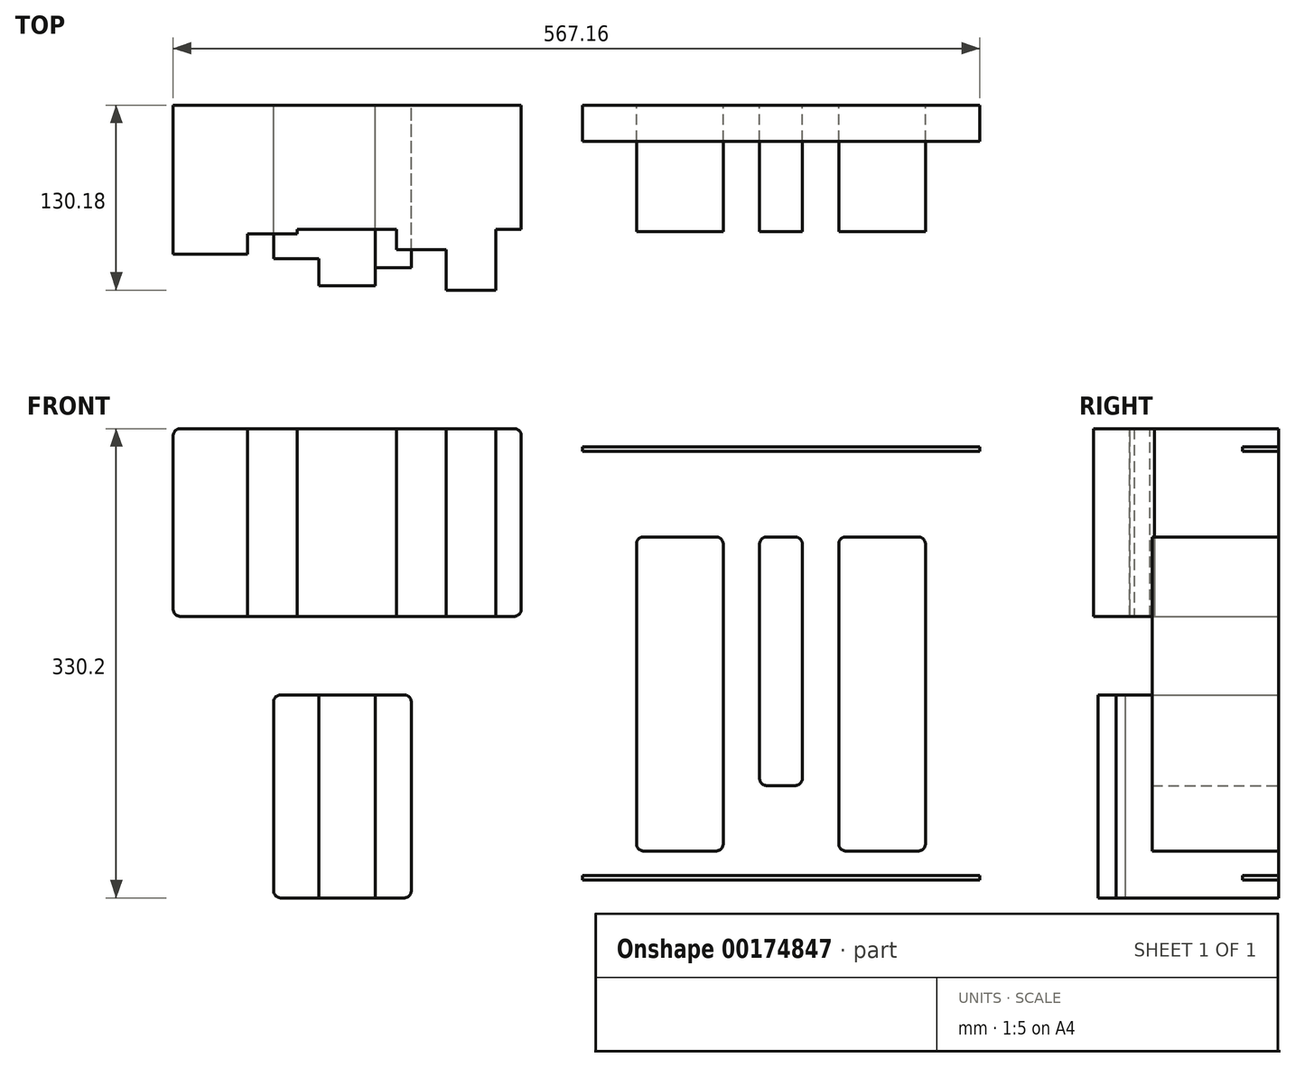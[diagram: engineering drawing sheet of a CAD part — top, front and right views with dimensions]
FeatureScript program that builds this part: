
annotation { "Feature Type Name" : "Feature", "Feature Type Description" : "" }
export const myFeature = defineFeature(function(context is Context, id is Id, definition is map)
    precondition{}
    {
        {
            var Q0;
            Q0=qCreatedBy(makeId("Front.planeOp"),FACE);
            var sketch = newSketch(context, id + "F0", { "sketchPlane" : qUnion([Q0])});
            skLineSegment(sketch, "E0.bottom", {"start": v(402.06, -139.7) * mm, "end": v(463.02, -139.7) * mm});
            skLineSegment(sketch, "E0.top", {"start": v(402.06, -360.68) * mm, "end": v(463.02, -360.68) * mm});
            skLineSegment(sketch, "E0.left", {"start": v(402.06, -139.7) * mm, "end": v(402.06, -360.68) * mm});
            skLineSegment(sketch, "E0.right", {"start": v(463.02, -139.7) * mm, "end": v(463.02, -360.68) * mm});
            skLineSegment(sketch, "E1.bottom", {"start": v(544.3, -139.7) * mm, "end": v(605.26, -139.7) * mm});
            skLineSegment(sketch, "E1.top", {"start": v(544.3, -360.68) * mm, "end": v(605.26, -360.68) * mm});
            skLineSegment(sketch, "E1.left", {"start": v(544.3, -139.7) * mm, "end": v(544.3, -360.68) * mm});
            skLineSegment(sketch, "E1.right", {"start": v(605.26, -139.7) * mm, "end": v(605.26, -360.68) * mm});
            skLineSegment(sketch, "E2.bottom", {"start": v(488.67, -139.7) * mm, "end": v(518.64, -139.7) * mm});
            skLineSegment(sketch, "E2.top", {"start": v(488.67, -314.7) * mm, "end": v(518.64, -314.7) * mm});
            skLineSegment(sketch, "E2.left", {"start": v(488.67, -139.7) * mm, "end": v(488.67, -314.7) * mm});
            skLineSegment(sketch, "E2.right", {"start": v(518.64, -139.7) * mm, "end": v(518.64, -314.7) * mm});
            skLineSegment(sketch, "E3.bottom", {"start": v(0, 0) * mm, "end": v(736.6, 0) * mm, "construction": true});
            skLineSegment(sketch, "E3.top", {"start": v(0, -457.2) * mm, "end": v(736.6, -457.2) * mm, "construction": true});
            skLineSegment(sketch, "E3.left", {"start": v(0, 0) * mm, "end": v(0, -457.2) * mm, "construction": true});
            skLineSegment(sketch, "E3.right", {"start": v(736.6, 0) * mm, "end": v(736.6, -457.2) * mm, "construction": true});
            skLineSegment(sketch, "E4.right", {"start": v(128.59, -195.58) * mm, "end": v(128.59, -63.5) * mm});
            skLineSegment(sketch, "E5.bottom", {"start": v(128.59, -63.5) * mm, "end": v(163.51, -63.5) * mm});
            skLineSegment(sketch, "E5.top", {"start": v(128.59, -195.58) * mm, "end": v(163.51, -195.58) * mm});
            skLineSegment(sketch, "E5.left", {"start": v(128.59, -63.5) * mm, "end": v(128.59, -195.58) * mm});
            skLineSegment(sketch, "E5.right", {"start": v(163.51, -63.5) * mm, "end": v(163.51, -195.58) * mm});
            skLineSegment(sketch, "E6.bottom", {"start": v(163.51, -63.5) * mm, "end": v(233.36, -63.5) * mm});
            skLineSegment(sketch, "E6.top", {"start": v(163.51, -195.58) * mm, "end": v(233.36, -195.58) * mm});
            skLineSegment(sketch, "E6.right", {"start": v(233.36, -63.5) * mm, "end": v(233.36, -195.58) * mm});
            skLineSegment(sketch, "E7.bottom", {"start": v(233.36, -63.5) * mm, "end": v(268.29, -63.5) * mm});
            skLineSegment(sketch, "E7.top", {"start": v(233.36, -195.58) * mm, "end": v(268.29, -195.58) * mm});
            skLineSegment(sketch, "E7.right", {"start": v(268.29, -63.5) * mm, "end": v(268.29, -195.58) * mm});
            skLineSegment(sketch, "E8.bottom", {"start": v(268.29, -63.5) * mm, "end": v(303.21, -63.5) * mm});
            skLineSegment(sketch, "E8.top", {"start": v(268.29, -195.58) * mm, "end": v(303.21, -195.58) * mm});
            skLineSegment(sketch, "E8.right", {"start": v(303.21, -63.5) * mm, "end": v(303.21, -195.58) * mm});
            skLineSegment(sketch, "E9.bottom", {"start": v(303.21, -63.5) * mm, "end": v(321, -63.5) * mm});
            skLineSegment(sketch, "E9.top", {"start": v(303.21, -195.58) * mm, "end": v(321, -195.58) * mm});
            skLineSegment(sketch, "E9.right", {"start": v(321, -63.5) * mm, "end": v(321, -195.58) * mm});
            skPoint(sketch, "E10", {"position": v(50.8, -50.8) * mm});
            skLineSegment(sketch, "E11.bottom", {"start": v(128.59, -63.5) * mm, "end": v(76.2, -63.5) * mm});
            skLineSegment(sketch, "E11.top", {"start": v(128.59, -195.58) * mm, "end": v(76.2, -195.58) * mm});
            skLineSegment(sketch, "E11.right", {"start": v(76.2, -63.5) * mm, "end": v(76.2, -195.58) * mm});
            skPoint(sketch, "E12", {"position": v(685.8, -50.8) * mm});
            skLineSegment(sketch, "E13.bottom", {"start": v(146.84, -250.83) * mm, "end": v(178.59, -250.83) * mm});
            skLineSegment(sketch, "E13.top", {"start": v(146.84, -393.7) * mm, "end": v(178.59, -393.7) * mm});
            skLineSegment(sketch, "E13.left", {"start": v(146.84, -250.83) * mm, "end": v(146.84, -393.7) * mm});
            skLineSegment(sketch, "E13.right", {"start": v(178.59, -250.83) * mm, "end": v(178.59, -393.7) * mm});
            skLineSegment(sketch, "E14.bottom", {"start": v(178.59, -250.83) * mm, "end": v(218.27, -250.83) * mm});
            skLineSegment(sketch, "E14.top", {"start": v(178.59, -393.7) * mm, "end": v(218.27, -393.7) * mm});
            skLineSegment(sketch, "E14.right", {"start": v(218.27, -250.83) * mm, "end": v(218.27, -393.7) * mm});
            skLineSegment(sketch, "E15.bottom", {"start": v(218.27, -250.83) * mm, "end": v(243.67, -250.83) * mm});
            skLineSegment(sketch, "E15.top", {"start": v(218.27, -393.7) * mm, "end": v(243.67, -393.7) * mm});
            skLineSegment(sketch, "E15.right", {"start": v(243.67, -250.83) * mm, "end": v(243.67, -393.7) * mm});
            skPoint(sketch, "E16", {"position": v(50.8, -406.4) * mm});
            skPoint(sketch, "E17", {"position": v(685.8, -406.4) * mm});
            skSolve(sketch);
        }
        {
            var Q0;
            Q0=makeQuery(id+"F0.imprint","IMPRINT",FACE,{"disambiguationData":[TD([[makeQuery(id+"F0.imprint","IMPRINT",EDGE,{"derivedFrom":sQuery(id+"F0.wireOp",EDGE,"E0.bottom")}),-1.0]])]});
            var Q1;
            Q1=makeQuery(id+"F0.imprint","IMPRINT",FACE,{"disambiguationData":[TD([[makeQuery(id+"F0.imprint","IMPRINT",EDGE,{"derivedFrom":sQuery(id+"F0.wireOp",EDGE,"E1.bottom")}),-1.0]])]});
            var Q2;
            Q2=makeQuery(id+"F0.imprint","IMPRINT",FACE,{"disambiguationData":[TD([[makeQuery(id+"F0.imprint","IMPRINT",EDGE,{"derivedFrom":sQuery(id+"F0.wireOp",EDGE,"E2.bottom")}),-1.0]])]});
            extrude(context, id + "F1", {"entities" : qUnion([Q0, Q1, Q2]), "depth" : 88.9 * mm});
        }
        {
            var Q0;
            Q0=makeQuery(id+"F1.opExtrude","SWEPT_EDGE",EDGE,{"disambiguationData":[OSD([sQuery(id+"F0.wireOp",EDGE,"E0.bottom"),sQuery(id+"F0.wireOp",EDGE,"E0.right")])]});
            var Q1;
            Q1=makeQuery(id+"F1.opExtrude","SWEPT_EDGE",EDGE,{"disambiguationData":[OSD([sQuery(id+"F0.wireOp",EDGE,"E2.bottom"),sQuery(id+"F0.wireOp",EDGE,"E2.right")])]});
            var Q2;
            Q2=makeQuery(id+"F1.opExtrude","SWEPT_EDGE",EDGE,{"disambiguationData":[OSD([sQuery(id+"F0.wireOp",EDGE,"E1.bottom"),sQuery(id+"F0.wireOp",EDGE,"E1.right")])]});
            var Q3;
            Q3=makeQuery(id+"F1.opExtrude","SWEPT_EDGE",EDGE,{"disambiguationData":[OSD([sQuery(id+"F0.wireOp",EDGE,"E1.bottom"),sQuery(id+"F0.wireOp",EDGE,"E1.left")])]});
            var Q4;
            Q4=makeQuery(id+"F1.opExtrude","SWEPT_EDGE",EDGE,{"disambiguationData":[OSD([sQuery(id+"F0.wireOp",EDGE,"E0.bottom"),sQuery(id+"F0.wireOp",EDGE,"E0.left")])]});
            var Q5;
            Q5=makeQuery(id+"F1.opExtrude","SWEPT_EDGE",EDGE,{"disambiguationData":[OSD([sQuery(id+"F0.wireOp",EDGE,"E0.top"),sQuery(id+"F0.wireOp",EDGE,"E0.left")])]});
            var Q6;
            Q6=makeQuery(id+"F1.opExtrude","SWEPT_EDGE",EDGE,{"disambiguationData":[OSD([sQuery(id+"F0.wireOp",EDGE,"E2.top"),sQuery(id+"F0.wireOp",EDGE,"E2.left")])]});
            var Q7;
            Q7=makeQuery(id+"F1.opExtrude","SWEPT_EDGE",EDGE,{"disambiguationData":[OSD([sQuery(id+"F0.wireOp",EDGE,"E1.top"),sQuery(id+"F0.wireOp",EDGE,"E1.left")])]});
            var Q8;
            Q8=makeQuery(id+"F1.opExtrude","SWEPT_EDGE",EDGE,{"disambiguationData":[OSD([sQuery(id+"F0.wireOp",EDGE,"E0.top"),sQuery(id+"F0.wireOp",EDGE,"E0.right")])]});
            var Q9;
            Q9=makeQuery(id+"F1.opExtrude","SWEPT_EDGE",EDGE,{"disambiguationData":[OSD([sQuery(id+"F0.wireOp",EDGE,"E2.top"),sQuery(id+"F0.wireOp",EDGE,"E2.right")])]});
            var Q10;
            Q10=makeQuery(id+"F1.opExtrude","SWEPT_EDGE",EDGE,{"disambiguationData":[OSD([sQuery(id+"F0.wireOp",EDGE,"E1.top"),sQuery(id+"F0.wireOp",EDGE,"E1.right")])]});
            fillet(context, id + "F2", {"entities" : qUnion([Q0, Q1, Q2, Q3, Q4, Q5, Q6, Q7, Q8, Q9, Q10]), "radius" : 5.08 * mm, "tangentPropagation" : true, "allowEdgeOverflow" : false});
        }
        {
            var Q0;
            Q0=makeQuery(id+"F1.opExtrude","SWEPT_EDGE",EDGE,{"disambiguationData":[OSD([sQuery(id+"F0.wireOp",EDGE,"E2.bottom"),sQuery(id+"F0.wireOp",EDGE,"E2.left")])]});
            var Q1;
            Q1=makeQuery(id+"FXifytqj1vpHj8I_2.opExtrude","SWEPT_EDGE",EDGE,{"disambiguationData":[OSD([sQuery(id+"F0.wireOp",EDGE,"VYxTvCZB-CYbp-Cyqk-qKJR-zw5bBLdlwLOv.top"),sQuery(id+"F0.wireOp",EDGE,"VYxTvCZB-CYbp-Cyqk-qKJR-zw5bBLdlwLOv.left")])]});
            var Q2;
            Q2=makeQuery(id+"FXifytqj1vpHj8I_2.opExtrude","SWEPT_EDGE",EDGE,{"disambiguationData":[OSD([sQuery(id+"F0.wireOp",EDGE,"VYxTvCZB-CYbp-Cyqk-qKJR-zw5bBLdlwLOv.bottom"),sQuery(id+"F0.wireOp",EDGE,"VYxTvCZB-CYbp-Cyqk-qKJR-zw5bBLdlwLOv.left")])]});
            var Q3;
            Q3=makeQuery(id+"FB6OAgb9by0tff1_1.opExtrude","SWEPT_EDGE",EDGE,{"disambiguationData":[OSD([sQuery(id+"F0.wireOp",EDGE,"04hokktK-nRdH-FnVl-lkE3-cBnQYboMP6h8.top"),sQuery(id+"F0.wireOp",EDGE,"04hokktK-nRdH-FnVl-lkE3-cBnQYboMP6h8.right")])]});
            var Q4;
            Q4=makeQuery(id+"FXifytqj1vpHj8I_2.opExtrude","SWEPT_EDGE",EDGE,{"disambiguationData":[OSD([sQuery(id+"F0.wireOp",EDGE,"VYxTvCZB-CYbp-Cyqk-qKJR-zw5bBLdlwLOv.bottom"),sQuery(id+"F0.wireOp",EDGE,"VYxTvCZB-CYbp-Cyqk-qKJR-zw5bBLdlwLOv.right")])]});
            var Q5;
            Q5=makeQuery(id+"FB6OAgb9by0tff1_1.opExtrude","SWEPT_EDGE",EDGE,{"disambiguationData":[OSD([sQuery(id+"F0.wireOp",EDGE,"04hokktK-nRdH-FnVl-lkE3-cBnQYboMP6h8.bottom"),sQuery(id+"F0.wireOp",EDGE,"04hokktK-nRdH-FnVl-lkE3-cBnQYboMP6h8.right")])]});
            var Q6;
            Q6=makeQuery(id+"FXifytqj1vpHj8I_2.opExtrude","SWEPT_EDGE",EDGE,{"disambiguationData":[OSD([sQuery(id+"F0.wireOp",EDGE,"VYxTvCZB-CYbp-Cyqk-qKJR-zw5bBLdlwLOv.top"),sQuery(id+"F0.wireOp",EDGE,"04hokktK-nRdH-FnVl-lkE3-cBnQYboMP6h8.bottom"),sQuery(id+"F0.wireOp",EDGE,"04hokktK-nRdH-FnVl-lkE3-cBnQYboMP6h8.left")])]});
            fillet(context, id + "F3", {"entities" : qUnion([Q0, Q1, Q2, Q3, Q4, Q5, Q6]), "radius" : 5.08 * mm, "tangentPropagation" : true, "allowEdgeOverflow" : false});
        }
        {
            var Q0;
            Q0=makeQuery(id+"F0.imprint","IMPRINT",FACE,{"disambiguationData":[TD([[makeQuery(id+"F0.imprint","IMPRINT",EDGE,{"derivedFrom":sQuery(id+"F0.wireOp",EDGE,"E11.bottom")}),1.0]])]});
            extrude(context, id + "F4", {"entities" : qUnion([Q0]), "depth" : 104.77 * mm});
        }
        {
            var Q0;
            Q0=makeQuery(id+"F0.imprint","IMPRINT",FACE,{"disambiguationData":[TD([[makeQuery(id+"F0.imprint","IMPRINT",EDGE,{"derivedFrom":sQuery(id+"F0.wireOp",EDGE,"E5.bottom")}),-1.0]])]});
            extrude(context, id + "F5", {"entities" : qUnion([Q0]), "operationType" : NewBodyOperationType.ADD, "depth" : 90.5 * mm});
        }
        {
            var Q0;
            Q0=makeQuery(id+"F0.imprint","IMPRINT",FACE,{"disambiguationData":[TD([[makeQuery(id+"F0.imprint","IMPRINT",EDGE,{"derivedFrom":sQuery(id+"F0.wireOp",EDGE,"E6.bottom")}),-1.0]])]});
            extrude(context, id + "F6", {"entities" : qUnion([Q0]), "operationType" : NewBodyOperationType.ADD, "depth" : 87.33 * mm});
        }
        {
            var Q0;
            Q0=makeQuery(id+"F0.imprint","IMPRINT",FACE,{"disambiguationData":[TD([[makeQuery(id+"F0.imprint","IMPRINT",EDGE,{"derivedFrom":sQuery(id+"F0.wireOp",EDGE,"E7.bottom")}),-1.0]])]});
            extrude(context, id + "F7", {"entities" : qUnion([Q0]), "operationType" : NewBodyOperationType.ADD, "depth" : 101.6 * mm});
        }
        {
            var Q0;
            Q0=makeQuery(id+"F0.imprint","IMPRINT",FACE,{"disambiguationData":[TD([[makeQuery(id+"F0.imprint","IMPRINT",EDGE,{"derivedFrom":sQuery(id+"F0.wireOp",EDGE,"E8.bottom")}),-1.0]])]});
            extrude(context, id + "F8", {"entities" : qUnion([Q0]), "operationType" : NewBodyOperationType.ADD, "depth" : 130.17 * mm});
        }
        {
            var Q0;
            Q0=makeQuery(id+"F0.imprint","IMPRINT",FACE,{"disambiguationData":[TD([[makeQuery(id+"F0.imprint","IMPRINT",EDGE,{"derivedFrom":sQuery(id+"F0.wireOp",EDGE,"E9.bottom")}),-1.0]])]});
            extrude(context, id + "F9", {"entities" : qUnion([Q0]), "operationType" : NewBodyOperationType.ADD, "depth" : 87.33 * mm});
        }
        {
            var Q0;
            Q0=makeQuery(id+"F0.imprint","IMPRINT",FACE,{"disambiguationData":[TD([[makeQuery(id+"F0.imprint","IMPRINT",EDGE,{"derivedFrom":sQuery(id+"F0.wireOp",EDGE,"E13.bottom")}),-1.0]])]});
            extrude(context, id + "F10", {"entities" : qUnion([Q0]), "depth" : 107.95 * mm});
        }
        {
            var Q0;
            Q0=makeQuery(id+"F0.imprint","IMPRINT",FACE,{"disambiguationData":[TD([[makeQuery(id+"F0.imprint","IMPRINT",EDGE,{"derivedFrom":sQuery(id+"F0.wireOp",EDGE,"E14.bottom")}),-1.0]])]});
            extrude(context, id + "F11", {"entities" : qUnion([Q0]), "operationType" : NewBodyOperationType.ADD, "depth" : 127 * mm});
        }
        {
            var Q0;
            Q0=makeQuery(id+"F0.imprint","IMPRINT",FACE,{"disambiguationData":[TD([[makeQuery(id+"F0.imprint","IMPRINT",EDGE,{"derivedFrom":sQuery(id+"F0.wireOp",EDGE,"E15.bottom")}),-1.0]])]});
            extrude(context, id + "F12", {"entities" : qUnion([Q0]), "depth" : 114.3 * mm});
        }
        {
            var Q0;
            Q0=qCreatedBy(makeId("Front.planeOp"),FACE);
            var sketch = newSketch(context, id + "F13", { "sketchPlane" : qUnion([Q0])});
            skLineSegment(sketch, "E18.bottom", {"start": v(363.96, -76.2) * mm, "end": v(643.36, -76.2) * mm});
            skLineSegment(sketch, "E18.top", {"start": v(363.96, -79.38) * mm, "end": v(643.36, -79.38) * mm});
            skLineSegment(sketch, "E18.left", {"start": v(363.96, -76.2) * mm, "end": v(363.96, -79.38) * mm});
            skLineSegment(sketch, "E18.right", {"start": v(643.36, -76.2) * mm, "end": v(643.36, -79.38) * mm});
            skLineSegment(sketch, "E19.bottom", {"start": v(363.96, -377.83) * mm, "end": v(643.36, -377.83) * mm});
            skLineSegment(sketch, "E19.top", {"start": v(363.96, -381) * mm, "end": v(643.36, -381) * mm});
            skLineSegment(sketch, "E19.left", {"start": v(363.96, -377.83) * mm, "end": v(363.96, -381) * mm});
            skLineSegment(sketch, "E19.right", {"start": v(643.36, -377.83) * mm, "end": v(643.36, -381) * mm});
            skSolve(sketch);
        }
        {
            var Q0;
            Q0=qSketchRegion(id+"F13",true);
            extrude(context, id + "F14", {"entities" : qUnion([Q0]), "depth" : 25.4 * mm});
        }
        {
            var Q0;
            Q0=makeQuery(id+"F9.opExtrude","SWEPT_EDGE",EDGE,{"disambiguationData":[OSD([sQuery(id+"F0.wireOp",EDGE,"E9.bottom"),sQuery(id+"F0.wireOp",EDGE,"E9.right")])]});
            var Q1;
            Q1=makeQuery(id+"F4.opExtrude","SWEPT_EDGE",EDGE,{"disambiguationData":[OSD([sQuery(id+"F0.wireOp",EDGE,"E11.bottom"),sQuery(id+"F0.wireOp",EDGE,"E11.right")])]});
            var Q2;
            Q2=makeQuery(id+"F9.opExtrude","SWEPT_EDGE",EDGE,{"disambiguationData":[OSD([sQuery(id+"F0.wireOp",EDGE,"E9.top"),sQuery(id+"F0.wireOp",EDGE,"E9.right")])]});
            var Q3;
            Q3=makeQuery(id+"F4.opExtrude","SWEPT_EDGE",EDGE,{"disambiguationData":[OSD([sQuery(id+"F0.wireOp",EDGE,"E11.top"),sQuery(id+"F0.wireOp",EDGE,"E11.right")])]});
            var Q4;
            Q4=makeQuery(id+"F10.opExtrude","SWEPT_EDGE",EDGE,{"disambiguationData":[OSD([sQuery(id+"F0.wireOp",EDGE,"E13.bottom"),sQuery(id+"F0.wireOp",EDGE,"E13.left")])]});
            var Q5;
            Q5=makeQuery(id+"F10.opExtrude","SWEPT_EDGE",EDGE,{"disambiguationData":[OSD([sQuery(id+"F0.wireOp",EDGE,"E13.top"),sQuery(id+"F0.wireOp",EDGE,"E13.left")])]});
            var Q6;
            Q6=makeQuery(id+"F12.opExtrude","SWEPT_EDGE",EDGE,{"disambiguationData":[OSD([sQuery(id+"F0.wireOp",EDGE,"E15.bottom"),sQuery(id+"F0.wireOp",EDGE,"E15.right")])]});
            var Q7;
            Q7=makeQuery(id+"F12.opExtrude","SWEPT_EDGE",EDGE,{"disambiguationData":[OSD([sQuery(id+"F0.wireOp",EDGE,"E15.top"),sQuery(id+"F0.wireOp",EDGE,"E15.right")])]});
            fillet(context, id + "F15", {"entities" : qUnion([Q0, Q1, Q2, Q3, Q4, Q5, Q6, Q7]), "radius" : 5.08 * mm, "tangentPropagation" : true, "allowEdgeOverflow" : false});
        }
    });
